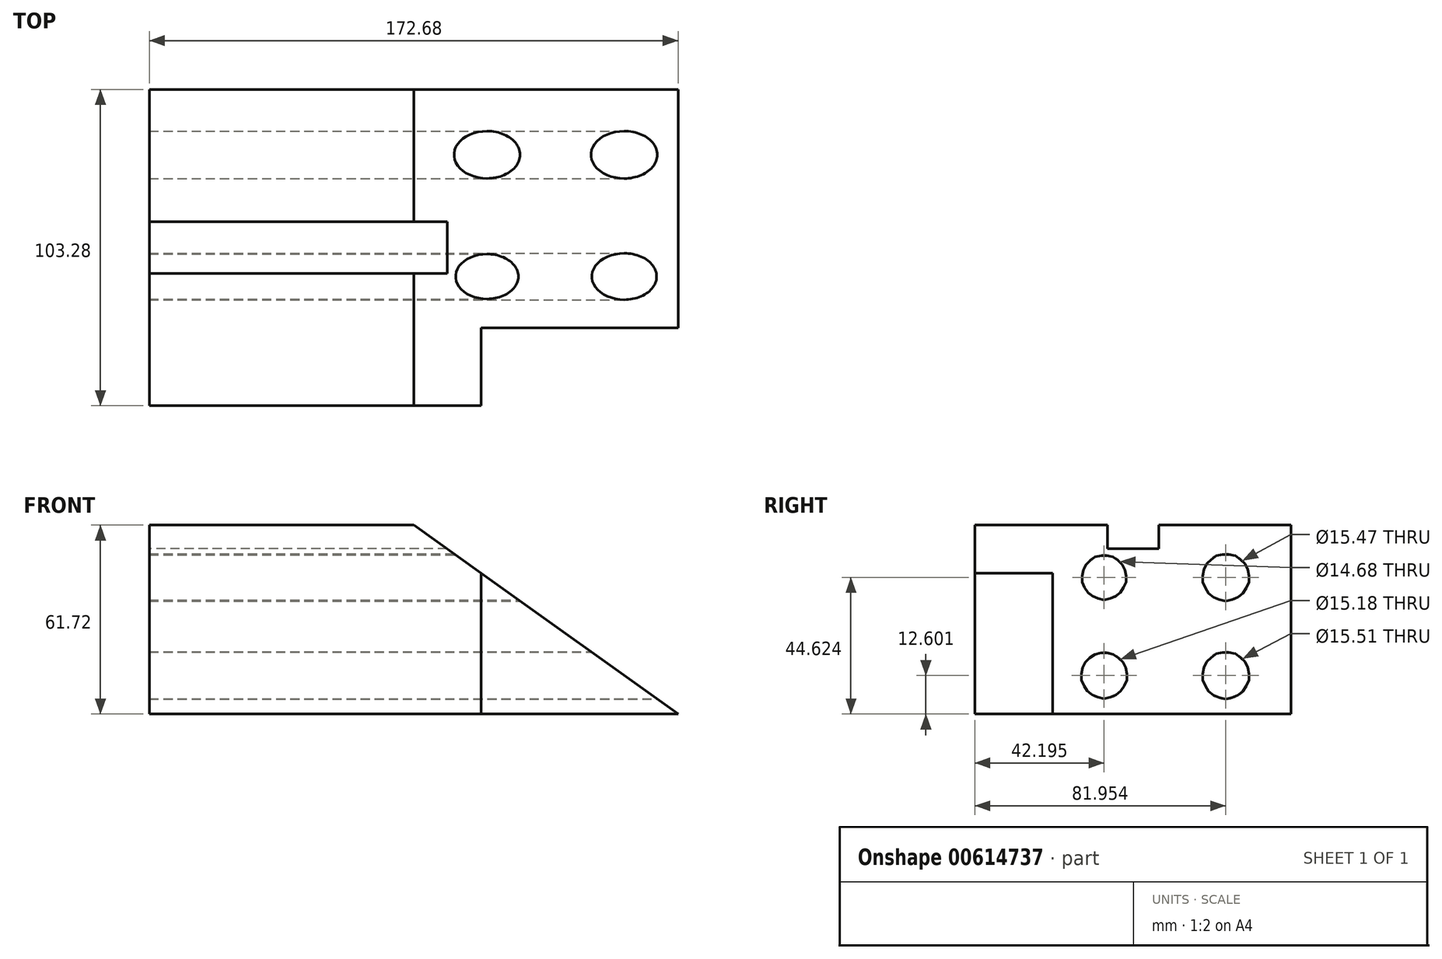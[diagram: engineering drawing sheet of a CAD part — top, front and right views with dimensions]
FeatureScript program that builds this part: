
annotation { "Feature Type Name" : "Feature", "Feature Type Description" : "" }
export const myFeature = defineFeature(function(context is Context, id is Id, definition is map)
    precondition{}
    {
        {
            var Q0;
            Q0=qCreatedBy(makeId("Top.planeOp"),FACE);
            var sketch = newSketch(context, id + "F0", { "sketchPlane" : qUnion([Q0])});
            skLineSegment(sketch, "E0.bottom", {"start": v(86.34, 51.64) * mm, "end": v(-86.34, 51.64) * mm});
            skLineSegment(sketch, "E0.top", {"start": v(86.34, -51.64) * mm, "end": v(-86.34, -51.64) * mm});
            skLineSegment(sketch, "E0.left", {"start": v(86.34, 51.64) * mm, "end": v(86.34, -51.64) * mm});
            skLineSegment(sketch, "E0.right", {"start": v(-86.34, 51.64) * mm, "end": v(-86.34, -51.64) * mm});
            skPoint(sketch, "E0.middle", {"position": v(0, 0) * mm});
            skSolve(sketch);
        }
        {
            var Q0;
            Q0=makeQuery(id+"F0.imprint","IMPRINT",FACE,{"disambiguationData":[TD([[makeQuery(id+"F0.imprint","IMPRINT",EDGE,{"derivedFrom":sQuery(id+"F0.wireOp",EDGE,"E0.bottom")}),1.0]])]});
            extrude(context, id + "F1", {"entities" : qUnion([Q0]), "depth" : 61.72 * mm, "offsetDistance" : 25.4 * mm});
        }
        {
            var Q0;
            Q0=makeQuery(id+"F1.opExtrude","SWEPT_FACE",FACE,{"disambiguationData":[OSD([sQuery(id+"F0.wireOp",EDGE,"E0.left")])]});
            var sketch = newSketch(context, id + "F2", { "sketchPlane" : qUnion([Q0])});
            skLineSegment(sketch, "E1.bottom", {"start": v(51.64, 61.72) * mm, "end": v(-30.13, 61.72) * mm});
            skLineSegment(sketch, "E1.top", {"start": v(51.64, 0) * mm, "end": v(-30.13, 0) * mm});
            skLineSegment(sketch, "E1.left", {"start": v(51.64, 61.72) * mm, "end": v(51.64, 0) * mm});
            skLineSegment(sketch, "E1.right", {"start": v(-30.13, 61.72) * mm, "end": v(-30.13, 0) * mm});
            skCircle(sketch, "E2", {"center": v(30.31, 12.6) * mm, "radius": 7.75 * mm});
            skCircle(sketch, "E3", {"center": v(30.31, 44.62) * mm, "radius": 7.74 * mm});
            skCircle(sketch, "E4", {"center": v(-9.45, 12.6) * mm, "radius": 7.6 * mm});
            skCircle(sketch, "E5", {"center": v(-9.45, 44.62) * mm, "radius": 7.34 * mm});
            skSolve(sketch);
        }
        {
            var Q0;
            Q0=makeQuery(id+"F2.imprint","IMPRINT",FACE,{"disambiguationData":[TD([[makeQuery(id+"F2.imprint","IMPRINT",EDGE,{"derivedFrom":sQuery(id+"F2.wireOp",EDGE,"E3")}),1.0]])]});
            var Q1;
            Q1=makeQuery(id+"F2.imprint","IMPRINT",FACE,{"disambiguationData":[TD([[makeQuery(id+"F2.imprint","IMPRINT",EDGE,{"derivedFrom":sQuery(id+"F2.wireOp",EDGE,"E5")}),1.0]])]});
            var Q2;
            Q2=makeQuery(id+"F2.imprint","IMPRINT",FACE,{"disambiguationData":[TD([[makeQuery(id+"F2.imprint","IMPRINT",EDGE,{"derivedFrom":sQuery(id+"F2.wireOp",EDGE,"E4")}),1.0]])]});
            var Q3;
            Q3=makeQuery(id+"F2.imprint","IMPRINT",FACE,{"disambiguationData":[TD([[makeQuery(id+"F2.imprint","IMPRINT",EDGE,{"derivedFrom":sQuery(id+"F2.wireOp",EDGE,"E2")}),1.0]])]});
            extrude(context, id + "F3", {"entities" : qUnion([Q0, Q1, Q2, Q3]), "operationType" : NewBodyOperationType.REMOVE, "oppositeDirection" : true, "depth" : 324.1 * mm, "offsetDistance" : 25.4 * mm});
        }
        {
            var Q0;
            Q0=makeQuery(id+"F1.opExtrude","SWEPT_FACE",FACE,{"disambiguationData":[OSD([sQuery(id+"F0.wireOp",EDGE,"E0.top")])]});
            var sketch = newSketch(context, id + "F4", { "sketchPlane" : qUnion([Q0])});
            skLineSegment(sketch, "E6", {"start": v(0, 61.72) * mm, "end": v(86.34, 0) * mm});
            skSolve(sketch);
        }
        {
            var Q0;
            {var subQ0=sQuery(id+"F4.wireOp",EDGE,"E6");Q0=makeQuery(id+"F4.imprint","IMPRINT",FACE,{"disambiguationData":[TD([[makeQuery(id+"F4.imprint","IMPRINT",EDGE,{"derivedFrom":subQ0}),1.0]])]});}
            extrude(context, id + "F5", {"entities" : qUnion([Q0]), "operationType" : NewBodyOperationType.REMOVE, "oppositeDirection" : true, "depth" : 152.4 * mm, "offsetDistance" : 25.4 * mm});
        }
        {
            var Q0;
            Q0=makeQuery(id+"F1.opExtrude","CAP_FACE",FACE,{"disambiguationData":[OSD([sQuery(id+"F0.wireOp",EDGE,"E0.bottom"),sQuery(id+"F0.wireOp",EDGE,"E0.top"),sQuery(id+"F0.wireOp",EDGE,"E0.left"),sQuery(id+"F0.wireOp",EDGE,"E0.right")])],"isStart":true});
            var sketch = newSketch(context, id + "F6", { "sketchPlane" : qUnion([Q0])});
            skLineSegment(sketch, "E7.bottom", {"start": v(86.34, 26.28) * mm, "end": v(21.99, 26.28) * mm});
            skLineSegment(sketch, "E7.top", {"start": v(86.34, 51.64) * mm, "end": v(21.99, 51.64) * mm});
            skLineSegment(sketch, "E7.left", {"start": v(86.34, 26.28) * mm, "end": v(86.34, 51.64) * mm});
            skLineSegment(sketch, "E7.right", {"start": v(21.99, 26.28) * mm, "end": v(21.99, 51.64) * mm});
            skSolve(sketch);
        }
        {
            var Q0;
            Q0=makeQuery(id+"F6.imprint","IMPRINT",FACE,{"disambiguationData":[TD([[makeQuery(id+"F6.imprint","IMPRINT",EDGE,{"derivedFrom":sQuery(id+"F6.wireOp",EDGE,"E7.bottom")}),-1.0]])]});
            extrude(context, id + "F7", {"entities" : qUnion([Q0]), "operationType" : NewBodyOperationType.REMOVE, "oppositeDirection" : true, "depth" : 75.44 * mm, "offsetDistance" : 25.4 * mm});
        }
        {
            var Q0;
            Q0=makeQuery(id+"F1.opExtrude","SWEPT_FACE",FACE,{"disambiguationData":[OSD([sQuery(id+"F0.wireOp",EDGE,"E0.right")])]});
            var sketch = newSketch(context, id + "F8", { "sketchPlane" : qUnion([Q0])});
            skLineSegment(sketch, "E8.bottom", {"start": v(8.4, 53.93) * mm, "end": v(-8.4, 53.93) * mm});
            skLineSegment(sketch, "E8.top", {"start": v(8.4, 69.51) * mm, "end": v(-8.4, 69.51) * mm});
            skLineSegment(sketch, "E8.left", {"start": v(8.4, 53.93) * mm, "end": v(8.4, 69.51) * mm});
            skLineSegment(sketch, "E8.right", {"start": v(-8.4, 53.93) * mm, "end": v(-8.4, 69.51) * mm});
            skPoint(sketch, "E8.middle", {"position": v(0, 61.72) * mm});
            skSolve(sketch);
        }
        {
            var Q0;
            {var subQ0=sQuery(id+"F8.wireOp",EDGE,"E8.bottom");Q0=makeQuery(id+"F8.imprint","IMPRINT",FACE,{"disambiguationData":[TD([[makeQuery(id+"F8.imprint","IMPRINT",EDGE,{"derivedFrom":subQ0}),-1.0]])]});}
            extrude(context, id + "F9", {"entities" : qUnion([Q0]), "operationType" : NewBodyOperationType.REMOVE, "oppositeDirection" : true, "depth" : 109.73 * mm, "offsetDistance" : 25.4 * mm});
        }
    });
